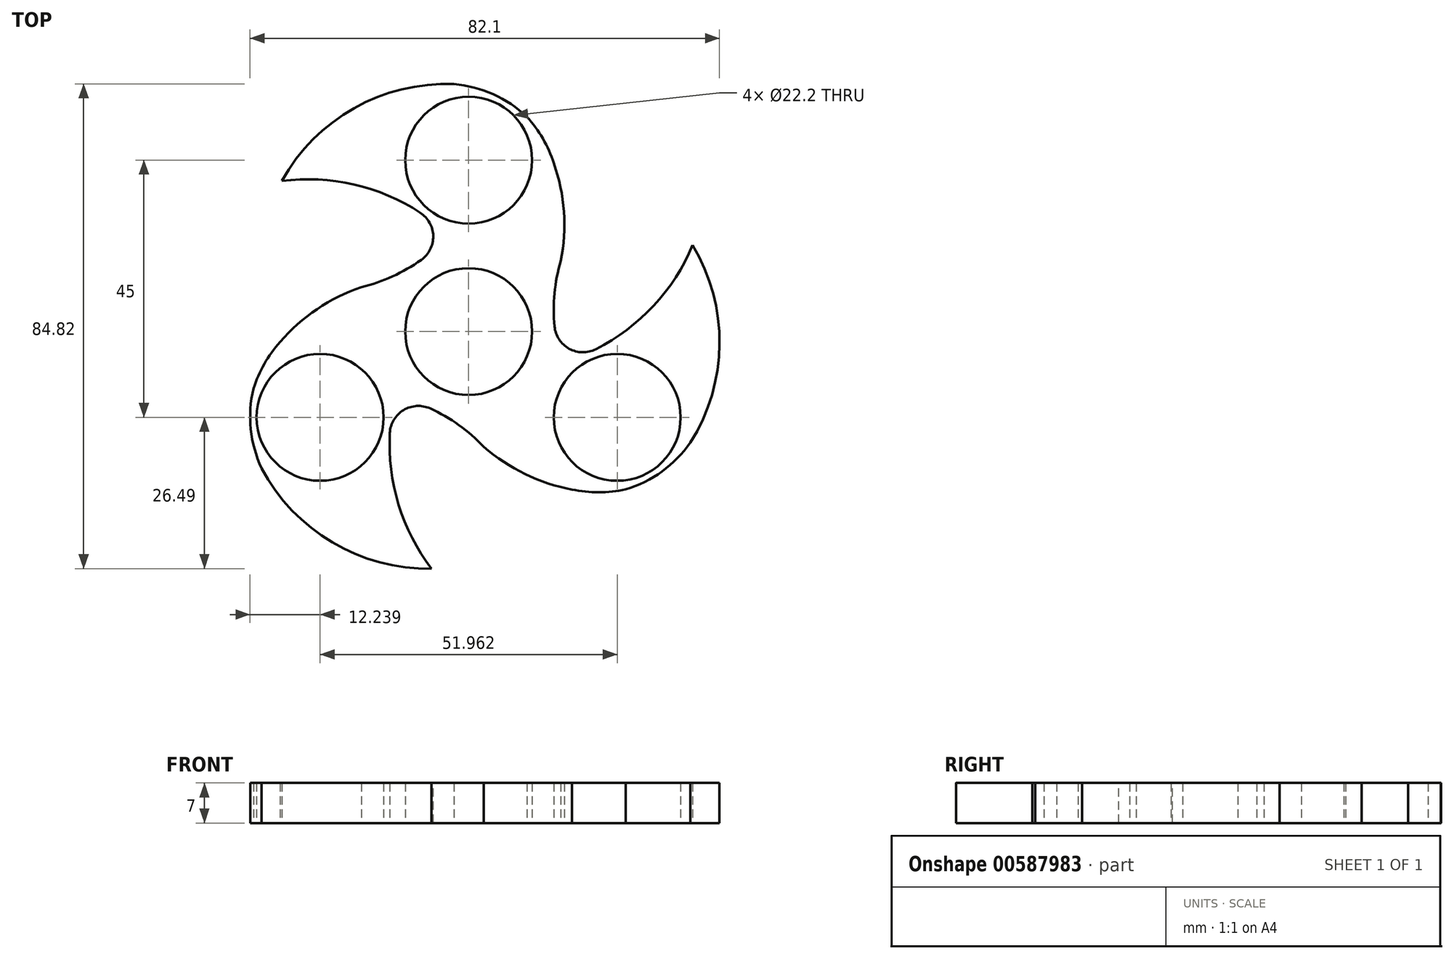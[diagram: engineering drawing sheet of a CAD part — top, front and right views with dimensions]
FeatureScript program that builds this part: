
annotation { "Feature Type Name" : "Feature", "Feature Type Description" : "" }
export const myFeature = defineFeature(function(context is Context, id is Id, definition is map)
    precondition{}
    {
        {
            var Q0;
            Q0=qCreatedBy(makeId("Top.planeOp"),FACE);
            var sketch = newSketch(context, id + "F0", { "sketchPlane" : qUnion([Q0])});
            skCircle(sketch, "E0", {"center": v(0, 0) * mm, "radius": 11.1 * mm});
            skCircle(sketch, "E1", {"center": v(0, 30) * mm, "radius": 11.1 * mm});
            skCircle(sketch, "E2.1.0", {"center": v(25.98, -15) * mm, "radius": 11.1 * mm});
            skCircle(sketch, "E2.2.0", {"center": v(-25.98, -15) * mm, "radius": 11.1 * mm});
            skArc(sketch, "E3", {"start": v(-2.59, 43.3) * mm, "mid": v(-20.03, 39.1) * mm, "end": v(-32.68, 26.37) * mm});
            skArc(sketch, "E4", {"start": v(-3.46, 16.87) * mm, "mid": v(-17, 24.9) * mm, "end": v(-32.68, 26.37) * mm});
            skArc(sketch, "E5.1.0", {"start": v(-36.2, -23.9) * mm, "mid": v(-23.84, -36.9) * mm, "end": v(-6.5, -41.48) * mm});
            skArc(sketch, "E5.1.1", {"start": v(-12.87, -11.43) * mm, "mid": v(-13.06, -27.17) * mm, "end": v(-6.5, -41.48) * mm});
            skArc(sketch, "E5.2.0", {"start": v(38.8, -19.4) * mm, "mid": v(43.87, -2.2) * mm, "end": v(39.17, 15.12) * mm});
            skArc(sketch, "E5.2.1", {"start": v(16.34, -5.43) * mm, "mid": v(30.06, 2.28) * mm, "end": v(39.17, 15.12) * mm});
            skArc(sketch, "E6", {"start": v(-18.78, 7.78) * mm, "mid": v(-10.43, 11.15) * mm, "end": v(-3.46, 16.87) * mm});
            skArc(sketch, "E7.trimOffspring", {"start": v(-18.78, 7.78) * mm, "mid": v(-26.52, 3.93) * mm, "end": v(-32.97, -1.83) * mm});
            skArc(sketch, "E8.1.0", {"start": v(2.65, -20.16) * mm, "mid": v(-4.44, -14.61) * mm, "end": v(-12.87, -11.43) * mm});
            skArc(sketch, "E8.1.1", {"start": v(2.65, -20.16) * mm, "mid": v(9.86, -24.93) * mm, "end": v(18.07, -27.64) * mm});
            skArc(sketch, "E8.2.0", {"start": v(16.13, 12.38) * mm, "mid": v(14.88, 3.46) * mm, "end": v(16.34, -5.43) * mm});
            skArc(sketch, "E8.2.1", {"start": v(16.13, 12.38) * mm, "mid": v(16.66, 21) * mm, "end": v(14.9, 29.47) * mm});
            skPoint(sketch, "E9.orphan", {"position": v(0, 13.1) * mm});
            skPoint(sketch, "E10.orphan", {"position": v(11.34, -6.55) * mm});
            skPoint(sketch, "E11.orphan", {"position": v(-11.34, -6.55) * mm});
            skArc(sketch, "E12", {"start": v(10.19, 37.59) * mm, "mid": v(4.28, 41.53) * mm, "end": v(-2.59, 43.3) * mm});
            skPoint(sketch, "E13.orphan", {"position": v(0, 43.1) * mm});
            skPoint(sketch, "E14.orphan", {"position": v(10.73, 37.51) * mm});
            skArc(sketch, "E15.1.0", {"start": v(-37.64, -9.97) * mm, "mid": v(-38.1, -17.05) * mm, "end": v(-36.2, -23.9) * mm});
            skArc(sketch, "E15.2.0", {"start": v(27.46, -27.62) * mm, "mid": v(33.82, -24.47) * mm, "end": v(38.8, -19.4) * mm});
            skPoint(sketch, "E16.orphan", {"position": v(27.12, -28.05) * mm});
            skPoint(sketch, "E17.orphan", {"position": v(-37.33, -21.55) * mm});
            skArc(sketch, "E18", {"start": v(-32.97, -1.83) * mm, "mid": v(-35.74, -5.65) * mm, "end": v(-37.64, -9.97) * mm});
            skPoint(sketch, "E19.orphan", {"position": v(-36.95, -7.64) * mm});
            skArc(sketch, "E20.1.0", {"start": v(18.07, -27.64) * mm, "mid": v(22.77, -28.13) * mm, "end": v(27.46, -27.62) * mm});
            skArc(sketch, "E20.2.0", {"start": v(14.9, 29.47) * mm, "mid": v(12.98, 33.78) * mm, "end": v(10.19, 37.59) * mm});
            skPoint(sketch, "E21.orphan", {"position": v(25.1, -28.18) * mm});
            skPoint(sketch, "E22.orphan", {"position": v(11.86, 35.82) * mm});
            skSolve(sketch);
        }
        {
            var Q0;
            Q0=makeQuery(id+"F0.imprint","IMPRINT",FACE,{"disambiguationData":[TD([[makeQuery(id+"F0.imprint","IMPRINT",EDGE,{"derivedFrom":sQuery(id+"F0.wireOp",EDGE,"E0")}),-1.0]])]});
            extrude(context, id + "F1", {"entities" : qUnion([Q0]), "depth" : 7 * mm, "offsetDistance" : 25 * mm});
        }
        {
            var Q0;
            Q0=makeQuery(id+"F1.opExtrude","SWEPT_EDGE",EDGE,{"disambiguationData":[OSD([sQuery(id+"F0.wireOp",EDGE,"E5.2.1"),sQuery(id+"F0.wireOp",EDGE,"E8.2.0")])]});
            fillet(context, id + "F2", {"entities" : qUnion([Q0]), "radius" : 5 * mm, "tangentPropagation" : true, "allowEdgeOverflow" : false});
        }
        {
            var Q0;
            Q0=makeQuery(id+"F1.opExtrude","SWEPT_EDGE",EDGE,{"disambiguationData":[OSD([sQuery(id+"F0.wireOp",EDGE,"E4"),sQuery(id+"F0.wireOp",EDGE,"E6")])]});
            fillet(context, id + "F3", {"entities" : qUnion([Q0]), "radius" : 5 * mm, "tangentPropagation" : true, "allowEdgeOverflow" : false});
        }
        {
            var Q0;
            Q0=makeQuery(id+"F1.opExtrude","SWEPT_EDGE",EDGE,{"disambiguationData":[OSD([sQuery(id+"F0.wireOp",EDGE,"E5.1.1"),sQuery(id+"F0.wireOp",EDGE,"E8.1.0")])]});
            fillet(context, id + "F4", {"entities" : qUnion([Q0]), "radius" : 5 * mm, "tangentPropagation" : true, "allowEdgeOverflow" : false});
        }
    });
